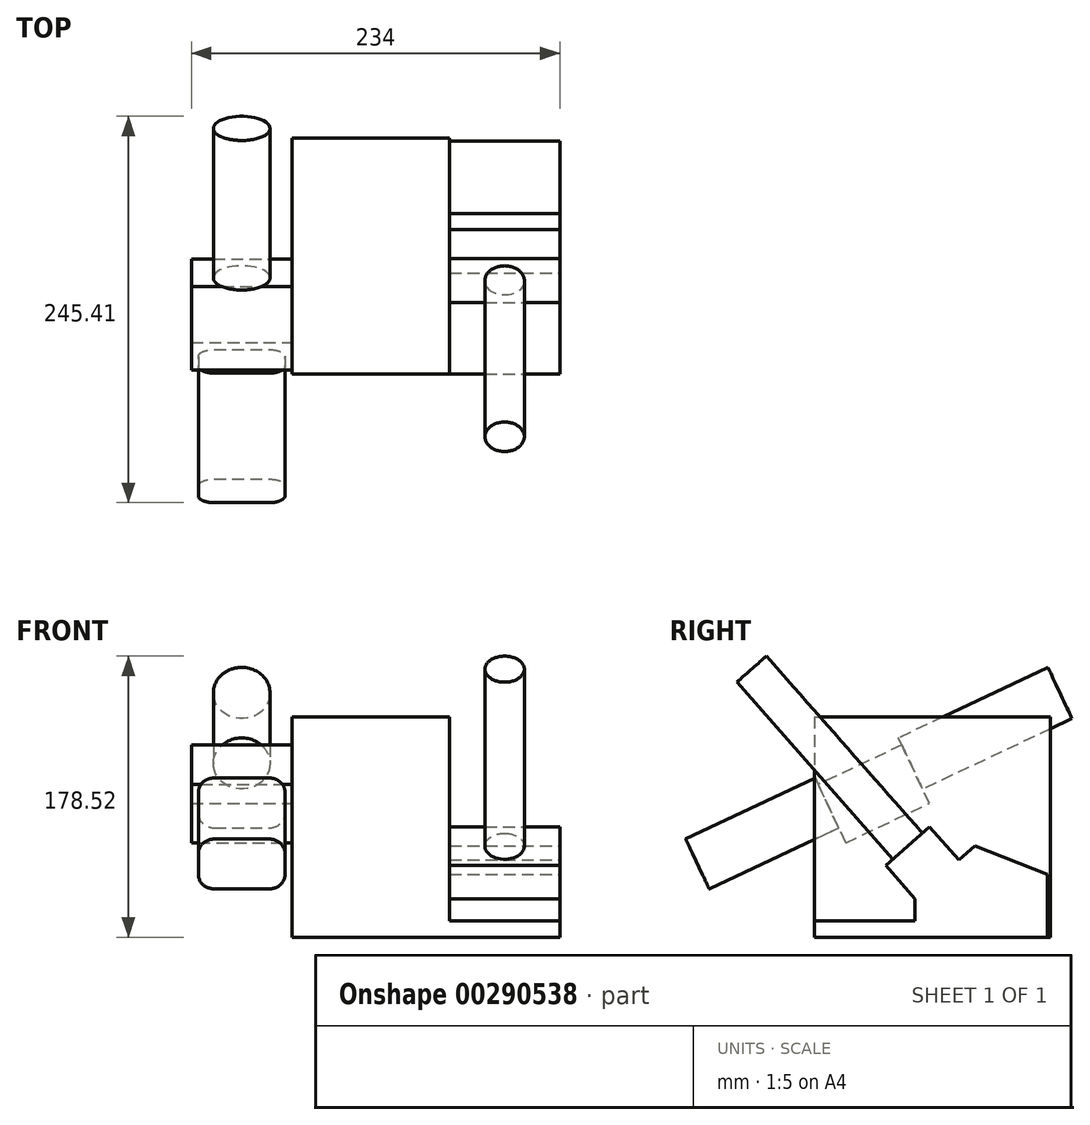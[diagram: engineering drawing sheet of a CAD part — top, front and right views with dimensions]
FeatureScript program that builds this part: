
annotation { "Feature Type Name" : "Feature", "Feature Type Description" : "" }
export const myFeature = defineFeature(function(context is Context, id is Id, definition is map)
    precondition{}
    {
        {
            var Q0;
            Q0=qCreatedBy(makeId("Top.planeOp"),FACE);
            var sketch = newSketch(context, id + "F0", { "sketchPlane" : qUnion([Q0])});
            skLineSegment(sketch, "E0.bottom", {"start": v(50, -75) * mm, "end": v(-50, -75) * mm});
            skLineSegment(sketch, "E0.top", {"start": v(50, 75) * mm, "end": v(-50, 75) * mm});
            skLineSegment(sketch, "E0.left", {"start": v(50, -75) * mm, "end": v(50, 75) * mm});
            skLineSegment(sketch, "E0.right", {"start": v(-50, -75) * mm, "end": v(-50, 75) * mm});
            skPoint(sketch, "E0.middle", {"position": v(0, 0) * mm});
            skSolve(sketch);
        }
        {
            var Q0;
            Q0 = qSketchRegion(id + "F0", true);
            extrude(context, id + "F1", {"entities" : qUnion([Q0]), "depth" : 140 * mm});
        }
        {
            var Q0;
            Q0=qCreatedBy(makeId("Top.planeOp"),FACE);
            var sketch = newSketch(context, id + "F2", { "sketchPlane" : qUnion([Q0])});
            skLineSegment(sketch, "E1.0", {"start": v(50, -75) * mm, "end": v(50, 75) * mm, "construction": true});
            skLineSegment(sketch, "E2.0", {"start": v(50, -75) * mm, "end": v(-50, -75) * mm, "construction": true});
            skLineSegment(sketch, "E3.bottom", {"start": v(50, -75) * mm, "end": v(120, -75) * mm});
            skLineSegment(sketch, "E3.top", {"start": v(50, 73) * mm, "end": v(120, 73) * mm});
            skLineSegment(sketch, "E3.left", {"start": v(50, -75) * mm, "end": v(50, 73) * mm});
            skLineSegment(sketch, "E3.right", {"start": v(120, -75) * mm, "end": v(120, 73) * mm});
            skSolve(sketch);
        }
        {
            var Q0;
            Q0 = qSketchRegion(id + "F2", true);
            extrude(context, id + "F3", {"entities" : qUnion([Q0]), "operationType" : NewBodyOperationType.ADD, "depth" : 85 * mm});
        }
        {
            var Q0;
            Q0=makeQuery(id+"F3.opExtrude","SWEPT_FACE",FACE,{"disambiguationData":[OSD([sQuery(id+"F2.wireOp",EDGE,"E3.right")])]});
            var sketch = newSketch(context, id + "F4", { "sketchPlane" : qUnion([Q0])});
            skLineSegment(sketch, "E4", {"start": v(73, 0) * mm, "end": v(27, 0) * mm, "construction": true});
            skLineSegment(sketch, "E5", {"start": v(27, 0) * mm, "end": v(27, 58) * mm, "construction": true});
            skLineSegment(sketch, "E6", {"start": v(73, 40) * mm, "end": v(27, 58) * mm});
            skLineSegment(sketch, "E7", {"start": v(73, 10.5) * mm, "end": v(-11, 10.5) * mm, "construction": true});
            skLineSegment(sketch, "E8", {"start": v(-11, 10.5) * mm, "end": v(-11, 24.5) * mm, "construction": true});
            skLineSegment(sketch, "E9", {"start": v(16.75, 48.97) * mm, "end": v(27, 58) * mm});
            skLineSegment(sketch, "E10", {"start": v(-11, 24.5) * mm, "end": v(-29.52, 45.5) * mm});
            skLineSegment(sketch, "E11", {"start": v(-29.52, 45.5) * mm, "end": v(-1.76, 69.97) * mm});
            skLineSegment(sketch, "E12", {"start": v(-1.76, 69.97) * mm, "end": v(16.75, 48.97) * mm});
            skLineSegment(sketch, "E13.0", {"start": v(-75, 85) * mm, "end": v(73, 85) * mm});
            skLineSegment(sketch, "E14", {"start": v(-11, 24.5) * mm, "end": v(-11, 10.5) * mm});
            skLineSegment(sketch, "E15", {"start": v(-11, 10.5) * mm, "end": v(-75, 10.5) * mm});
            skLineSegment(sketch, "E16", {"start": v(-75, 85) * mm, "end": v(-75, 10.5) * mm});
            skLineSegment(sketch, "E17", {"start": v(73, 85) * mm, "end": v(73, 40) * mm});
            skSolve(sketch);
        }
        {
            var Q0;
            Q0 = qSketchRegion(id + "F4", true);
            var Q1;
            Q1=makeQuery(id+"F1.opExtrude","SWEPT_FACE",FACE,{"disambiguationData":[OSD([sQuery(id+"F0.wireOp",EDGE,"E0.left")])]});
            extrude(context, id + "F5", {"entities" : qUnion([Q0]), "operationType" : NewBodyOperationType.REMOVE, "endBound" : BoundingType.UP_TO_SURFACE, "oppositeDirection" : true, "endBoundEntityFace" : qUnion([Q1]), "depth" : 25 * mm});
        }
        {
            var Q0;
            Q0=makeQuery(id+"F5.boolean.opBoolean","COPY",FACE,{"derivedFrom":makeQuery(id+"F5.opExtrude","SWEPT_FACE",FACE,{"disambiguationData":[OSD([sQuery(id+"F4.wireOp",EDGE,"E11")])]})});
            var sketch = newSketch(context, id + "F6", { "sketchPlane" : qUnion([Q0])});
            skLineSegment(sketch, "E18.0.0", {"start": v(50, 7.95) * mm, "end": v(120, 7.95) * mm, "construction": true});
            skLineSegment(sketch, "E18.0.1", {"start": v(120, 7.95) * mm, "end": v(120, 44.95) * mm, "construction": true});
            skLineSegment(sketch, "E18.0.2", {"start": v(120, 44.95) * mm, "end": v(50, 44.95) * mm, "construction": true});
            skLineSegment(sketch, "E18.0.3", {"start": v(50, 44.95) * mm, "end": v(50, 7.95) * mm, "construction": true});
            skLineSegment(sketch, "E19", {"start": v(85, 7.95) * mm, "end": v(85, 44.95) * mm, "construction": true});
            skCircle(sketch, "E20", {"center": v(85, 26.45) * mm, "radius": 12.5 * mm});
            skSolve(sketch);
        }
        {
            var Q0;
            Q0 = qSketchRegion(id + "F6", true);
            extrude(context, id + "F7", {"entities" : qUnion([Q0]), "operationType" : NewBodyOperationType.ADD, "depth" : 150 * mm});
        }
        {
            var Q0;
            Q0=makeQuery(id+"F1.opExtrude","SWEPT_FACE",FACE,{"disambiguationData":[OSD([sQuery(id+"F0.wireOp",EDGE,"E0.right")])]});
            var sketch = newSketch(context, id + "F8", { "sketchPlane" : qUnion([Q0])});
            skLineSegment(sketch, "E21", {"start": v(75, 0) * mm, "end": v(55, 0) * mm, "construction": true});
            skLineSegment(sketch, "E22", {"start": v(55, 0) * mm, "end": v(55, 60) * mm, "construction": true});
            skLineSegment(sketch, "E23", {"start": v(55, 60) * mm, "end": v(2, 60) * mm, "construction": true});
            skLineSegment(sketch, "E24", {"start": v(2, 60) * mm, "end": v(2, 85) * mm, "construction": true});
            skLineSegment(sketch, "E25", {"start": v(55, 60) * mm, "end": v(2, 85) * mm});
            skLineSegment(sketch, "E26", {"start": v(2, 85) * mm, "end": v(19.5, 122.08) * mm});
            skLineSegment(sketch, "E27", {"start": v(19.5, 122.08) * mm, "end": v(72.5, 97.08) * mm});
            skLineSegment(sketch, "E28", {"start": v(55, 60) * mm, "end": v(72.5, 97.08) * mm});
            skSolve(sketch);
        }
        {
            var Q0;
            Q0 = qSketchRegion(id + "F8", true);
            extrude(context, id + "F9", {"entities" : qUnion([Q0]), "operationType" : NewBodyOperationType.ADD, "depth" : 64 * mm});
        }
        {
            var Q0;
            Q0=makeQuery(id+"F9.opExtrude","SWEPT_FACE",FACE,{"disambiguationData":[OSD([sQuery(id+"F8.wireOp",EDGE,"E26")])]});
            var sketch = newSketch(context, id + "F10", { "sketchPlane" : qUnion([Q0])});
            skLineSegment(sketch, "E29.0.0", {"start": v(50, 118.73) * mm, "end": v(50, 77.73) * mm, "construction": true});
            skLineSegment(sketch, "E29.0.1", {"start": v(50, 77.73) * mm, "end": v(114, 77.73) * mm, "construction": true});
            skLineSegment(sketch, "E29.0.2", {"start": v(114, 77.73) * mm, "end": v(114, 118.73) * mm, "construction": true});
            skLineSegment(sketch, "E29.0.3", {"start": v(114, 118.73) * mm, "end": v(50, 118.73) * mm, "construction": true});
            skLineSegment(sketch, "E30", {"start": v(114, 77.73) * mm, "end": v(114, 105.73) * mm, "construction": true});
            skLineSegment(sketch, "E31", {"start": v(114, 105.73) * mm, "end": v(82, 105.73) * mm, "construction": true});
            skPoint(sketch, "E31.endSnap0", {"position": v(82, 77.73) * mm});
            skCircle(sketch, "E32", {"center": v(82, 105.73) * mm, "radius": 18 * mm});
            skSolve(sketch);
        }
        {
            var Q0;
            Q0 = qSketchRegion(id + "F10", true);
            extrude(context, id + "F11", {"entities" : qUnion([Q0]), "operationType" : NewBodyOperationType.ADD, "depth" : 105 * mm});
        }
        {
            var Q0;
            Q0=makeQuery(id+"F9.opExtrude","SWEPT_FACE",FACE,{"disambiguationData":[OSD([sQuery(id+"F8.wireOp",EDGE,"E28")])]});
            var sketch = newSketch(context, id + "F12", { "sketchPlane" : qUnion([Q0])});
            skArc(sketch, "E33.0.0", {"start": v(-69.55, 118.73) * mm, "mid": v(-82, 123.73) * mm, "end": v(-94.45, 118.73) * mm, "construction": true});
            skLineSegment(sketch, "E33.0.1", {"start": v(-94.45, 118.73) * mm, "end": v(-69.55, 118.73) * mm, "construction": true});
            skLineSegment(sketch, "E34", {"start": v(-82, 105.73) * mm, "end": v(-82, 88.23) * mm, "construction": true});
            skLineSegment(sketch, "E35", {"start": v(-82, 88.23) * mm, "end": v(-99.5, 88.23) * mm, "construction": true});
            skLineSegment(sketch, "E36.bottom", {"start": v(-109.5, 88.23) * mm, "end": v(-64.5, 88.23) * mm});
            skLineSegment(sketch, "E36.top", {"start": v(-99.5, 123.23) * mm, "end": v(-64.5, 123.23) * mm});
            skLineSegment(sketch, "E36.left", {"start": v(-109.5, 98.23) * mm, "end": v(-109.5, 113.23) * mm});
            skLineSegment(sketch, "E36.right", {"start": v(-54.5, 98.23) * mm, "end": v(-54.5, 113.23) * mm});
            skPoint(sketch, "E37.visualSharp", {"position": v(-109.5, 123.23) * mm});
            skArc(sketch, "E37.filletArc", {"start": v(-99.5, 123.23) * mm, "mid": v(-106.57, 120.3) * mm, "end": v(-109.5, 113.23) * mm});
            skPoint(sketch, "E38.visualSharp", {"position": v(-54.5, 123.23) * mm});
            skArc(sketch, "E38.filletArc", {"start": v(-54.5, 113.23) * mm, "mid": v(-57.43, 120.3) * mm, "end": v(-64.5, 123.23) * mm});
            skPoint(sketch, "E39.visualSharp", {"position": v(-109.5, 88.23) * mm});
            skArc(sketch, "E39.filletArc", {"start": v(-109.5, 98.23) * mm, "mid": v(-106.57, 91.16) * mm, "end": v(-99.5, 88.23) * mm});
            skPoint(sketch, "E40.visualSharp", {"position": v(-54.5, 88.23) * mm});
            skArc(sketch, "E40.filletArc", {"start": v(-64.5, 88.23) * mm, "mid": v(-57.43, 91.16) * mm, "end": v(-54.5, 98.23) * mm});
            skSolve(sketch);
        }
        {
            var Q0;
            Q0 = qSketchRegion(id + "F12", true);
            extrude(context, id + "F13", {"entities" : qUnion([Q0]), "operationType" : NewBodyOperationType.ADD, "depth" : 91 * mm});
        }
    });
